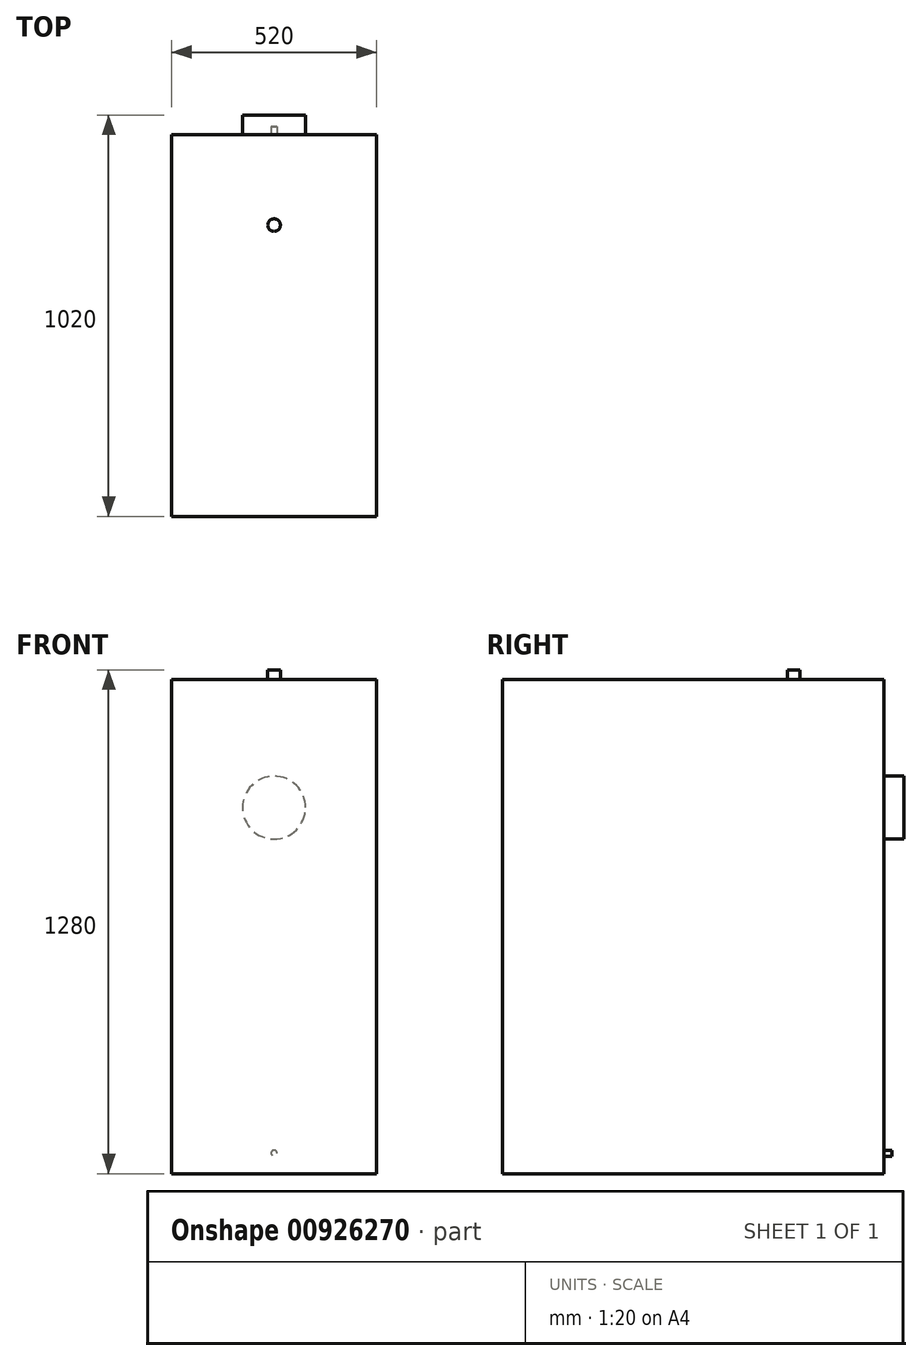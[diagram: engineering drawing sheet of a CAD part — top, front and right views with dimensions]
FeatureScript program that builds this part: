
annotation { "Feature Type Name" : "Feature", "Feature Type Description" : "" }
export const myFeature = defineFeature(function(context is Context, id is Id, definition is map)
    precondition{}
    {
        {
            var Q0;
            Q0=qCreatedBy(makeId("Top.planeOp"),FACE);
            var sketch = newSketch(context, id + "F0", { "sketchPlane" : qUnion([Q0])});
            skLineSegment(sketch, "E0.bottom", {"start": v(-260, 485) * mm, "end": v(260, 485) * mm});
            skLineSegment(sketch, "E0.top", {"start": v(-260, -485) * mm, "end": v(260, -485) * mm});
            skLineSegment(sketch, "E0.left", {"start": v(-260, 485) * mm, "end": v(-260, -485) * mm});
            skLineSegment(sketch, "E0.right", {"start": v(260, 485) * mm, "end": v(260, -485) * mm});
            skPoint(sketch, "E0.middle", {"position": v(0, 0) * mm});
            skSolve(sketch);
        }
        {
            var Q0;
            Q0=makeQuery(id+"F0.imprint","IMPRINT",FACE,{"disambiguationData":[TD([[makeQuery(id+"F0.imprint","IMPRINT",EDGE,{"derivedFrom":sQuery(id+"F0.wireOp",EDGE,"E0.bottom")}),-1.0]])]});
            extrude(context, id + "F1", {"entities" : qUnion([Q0]), "depth" : 1255 * mm, "offsetDistance" : 25 * mm});
        }
        {
            var Q0;
            Q0=makeQuery(id+"F1.opExtrude","SWEPT_FACE",FACE,{"disambiguationData":[OSD([sQuery(id+"F0.wireOp",EDGE,"E0.bottom")])]});
            var sketch = newSketch(context, id + "F2", { "sketchPlane" : qUnion([Q0])});
            skCircle(sketch, "E1", {"center": v(0, 930) * mm, "radius": 80 * mm});
            skCircle(sketch, "E2", {"center": v(0, 485) * mm, "radius": 16 * mm});
            skSolve(sketch);
        }
        {
            var Q0;
            Q0=makeQuery(id+"F2.imprint","IMPRINT",FACE,{"disambiguationData":[TD([[makeQuery(id+"F2.imprint","IMPRINT",EDGE,{"derivedFrom":sQuery(id+"F2.wireOp",EDGE,"E1")}),1.0]])]});
            extrude(context, id + "F3", {"entities" : qUnion([Q0]), "operationType" : NewBodyOperationType.ADD, "depth" : 50 * mm, "offsetDistance" : 25 * mm});
        }
        {
            var Q0;
            Q0=sQuery(id+"F2.wireOp",EDGE,"E2");
            extrude(context, id + "F4", {"bodyType" : ToolBodyType.SURFACE, "surfaceEntities" : qUnion([Q0]), "depth" : 25 * mm, "offsetDistance" : 25 * mm});
        }
        {
            var Q0;
            Q0=makeQuery(id+"F2.imprint","IMPRINT",FACE,{"disambiguationData":[TD([[makeQuery(id+"F2.imprint","IMPRINT",EDGE,{"derivedFrom":sQuery(id+"F2.wireOp",EDGE,"E1")}),-1.0]])]});
            var sketch = newSketch(context, id + "F5", { "sketchPlane" : qUnion([Q0])});
            skCircle(sketch, "E3", {"center": v(0, 52.05) * mm, "radius": 7.5 * mm});
            skSolve(sketch);
        }
        {
            var Q0;
            Q0 = qSketchRegion(id + "F5", true);
            extrude(context, id + "F6", {"entities" : qUnion([Q0]), "operationType" : NewBodyOperationType.ADD, "depth" : 20 * mm, "offsetDistance" : 25 * mm});
        }
        {
            var Q0;
            Q0=makeQuery(id+"F1.opExtrude","CAP_FACE",FACE,{"disambiguationData":[OSD([sQuery(id+"F0.wireOp",EDGE,"E0.bottom"),sQuery(id+"F0.wireOp",EDGE,"E0.top"),sQuery(id+"F0.wireOp",EDGE,"E0.left"),sQuery(id+"F0.wireOp",EDGE,"E0.right")])],"isStart":false});
            var sketch = newSketch(context, id + "F7", { "sketchPlane" : qUnion([Q0])});
            skCircle(sketch, "E4", {"center": v(0, 255) * mm, "radius": 16 * mm});
            skSolve(sketch);
        }
        {
            var Q0;
            Q0 = qSketchRegion(id + "F7", true);
            extrude(context, id + "F8", {"entities" : qUnion([Q0]), "operationType" : NewBodyOperationType.ADD, "depth" : 25 * mm, "offsetDistance" : 25 * mm});
        }
    });
